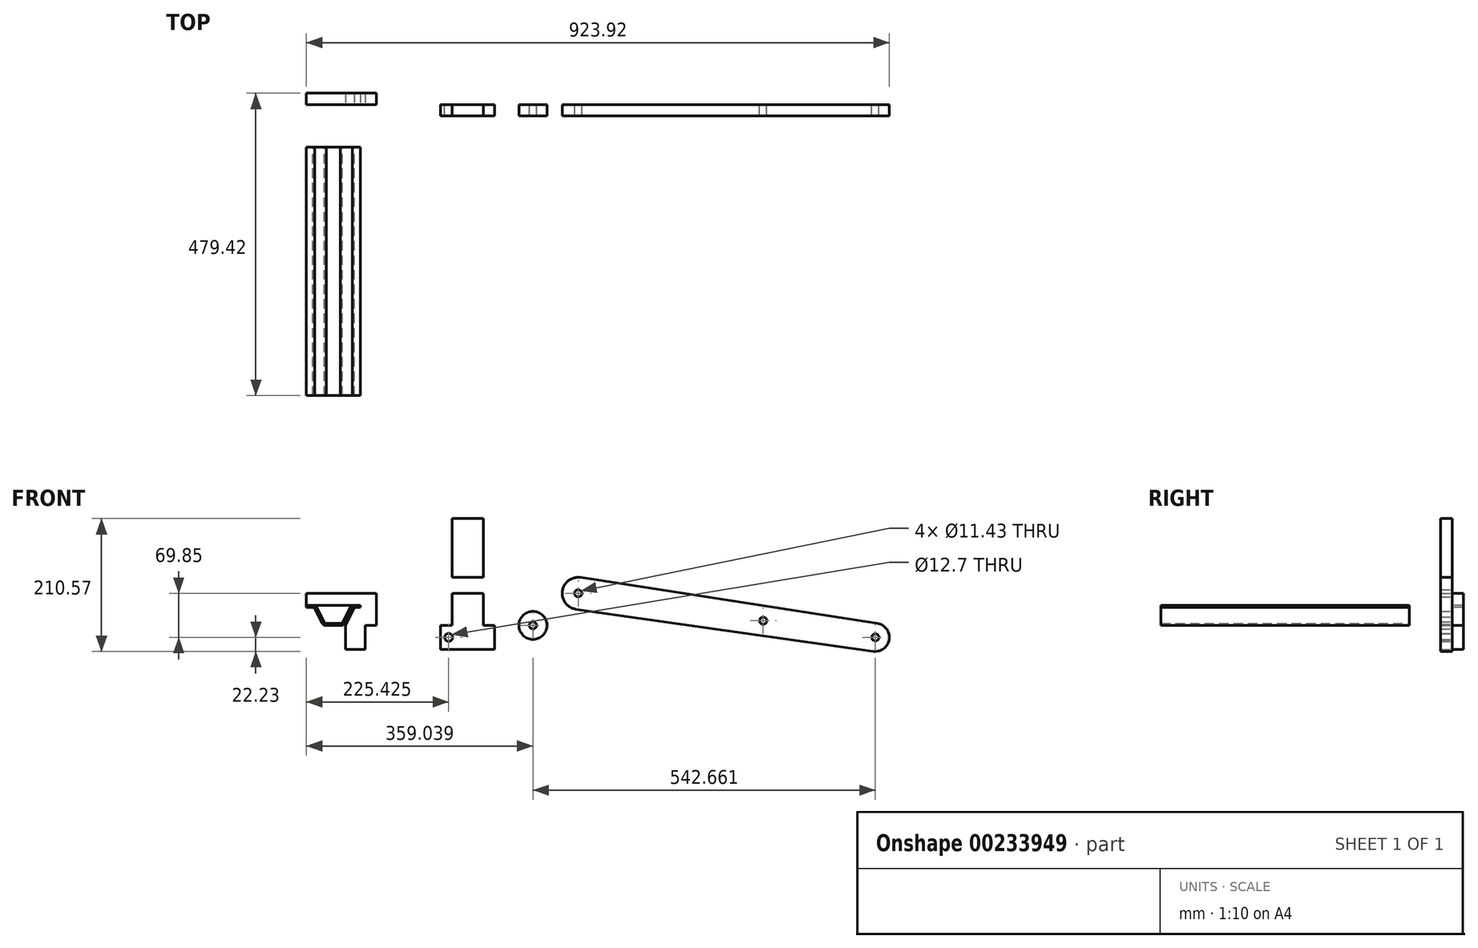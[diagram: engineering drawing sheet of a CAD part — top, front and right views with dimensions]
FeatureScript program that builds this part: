
annotation { "Feature Type Name" : "Feature", "Feature Type Description" : "" }
export const myFeature = defineFeature(function(context is Context, id is Id, definition is map)
    precondition{}
    {
        {
            var Q0;
            Q0=qCreatedBy(makeId("Top.planeOp"),FACE);
            var sketch = newSketch(context, id + "F0", { "sketchPlane" : qUnion([Q0])});
            skLineSegment(sketch, "E0.bottom", {"start": v(-241.3, 85.73) * mm, "end": v(-155.58, 85.73) * mm});
            skLineSegment(sketch, "E0.top", {"start": v(-241.3, 0) * mm, "end": v(-155.58, 0) * mm});
            skLineSegment(sketch, "E0.left", {"start": v(-241.3, 85.73) * mm, "end": v(-241.3, 0) * mm});
            skLineSegment(sketch, "E0.right", {"start": v(-155.58, 85.72) * mm, "end": v(-155.58, 0) * mm});
            skLineSegment(sketch, "E1", {"start": v(-212.73, 85.72) * mm, "end": v(-212.73, 0) * mm});
            skLineSegment(sketch, "E2", {"start": v(-184.15, 85.72) * mm, "end": v(-184.15, 0) * mm});
            skPoint(sketch, "E3", {"position": v(-198.44, 42.86) * mm});
            skPoint(sketch, "E3.positionSnap0", {"position": v(-198.44, 85.73) * mm});
            skPoint(sketch, "E3.positionSnap1", {"position": v(-241.3, 42.86) * mm});
            skLineSegment(sketch, "E4.bottom", {"start": v(-236.54, 52.39) * mm, "end": v(-231.2, 52.39) * mm});
            skLineSegment(sketch, "E4.top", {"start": v(-236.54, 42.86) * mm, "end": v(-231.2, 42.86) * mm});
            skLineSegment(sketch, "E4.left", {"start": v(-236.54, 52.39) * mm, "end": v(-236.54, 42.86) * mm});
            skLineSegment(sketch, "E4.right", {"start": v(-231.2, 52.39) * mm, "end": v(-231.2, 42.86) * mm});
            skLineSegment(sketch, "E5", {"start": v(-228.35, 85.73) * mm, "end": v(-228.35, 0) * mm});
            skLineSegment(sketch, "E6", {"start": v(-198.44, 85.73) * mm, "end": v(-198.44, 0) * mm, "construction": true});
            skLineSegment(sketch, "E7.MirrorCS", {"start": v(-165.67, 52.39) * mm, "end": v(-165.67, 42.86) * mm});
            skLineSegment(sketch, "E8.MirrorCS", {"start": v(-160.34, 52.39) * mm, "end": v(-160.34, 42.86) * mm});
            skPoint(sketch, "E9.MirrorP", {"position": v(-155.58, 42.86) * mm});
            skLineSegment(sketch, "E10.MirrorCS", {"start": v(-160.34, 52.39) * mm, "end": v(-165.67, 52.39) * mm});
            skLineSegment(sketch, "E11.MirrorCS", {"start": v(-160.34, 42.86) * mm, "end": v(-165.67, 42.86) * mm});
            skSolve(sketch);
        }
        {
            var Q0;
            {var subQ1=sQuery(id+"F0.wireOp",EDGE,"E0.left");Q0=makeQuery(id+"F0.imprint","IMPRINT",FACE,{"disambiguationData":[TD([[makeQuery(id+"F0.imprint","IMPRINT",EDGE,{"derivedFrom":subQ1}),1.0]])]});}
            var Q1;
            {var subQ0=sQuery(id+"F0.wireOp",EDGE,"E1");Q1=makeQuery(id+"F0.imprint","IMPRINT",FACE,{"disambiguationData":[TD([[makeQuery(id+"F0.imprint","IMPRINT",EDGE,{"derivedFrom":subQ0}),-1.0]])]});}
            var Q2;
            {var subQ0=sQuery(id+"F0.wireOp",EDGE,"E1");Q2=makeQuery(id+"F0.imprint","IMPRINT",FACE,{"disambiguationData":[TD([[makeQuery(id+"F0.imprint","IMPRINT",EDGE,{"derivedFrom":subQ0}),1.0]])]});}
            var Q3;
            {var subQ0=sQuery(id+"F0.wireOp",EDGE,"E0.right");Q3=makeQuery(id+"F0.imprint","IMPRINT",FACE,{"disambiguationData":[TD([[makeQuery(id+"F0.imprint","IMPRINT",EDGE,{"derivedFrom":subQ0}),-1.0]])]});}
            extrude(context, id + "F1", {"entities" : qUnion([Q0, Q1, Q2, Q3]), "depth" : 31.75 * mm});
        }
        {
            var Q0;
            Q0=makeQuery(id+"F1.opExtrude","SWEPT_FACE",FACE,{"disambiguationData":[OSD([sQuery(id+"F0.wireOp",EDGE,"E0.top")])]});
            var sketch = newSketch(context, id + "F2", { "sketchPlane" : qUnion([Q0])});
            skLineSegment(sketch, "E12", {"start": v(-241.3, 3.17) * mm, "end": v(-155.58, 3.18) * mm});
            skLineSegment(sketch, "E13", {"start": v(-241.3, 28.57) * mm, "end": v(-155.58, 28.57) * mm});
            skLineSegment(sketch, "E14", {"start": v(-228.35, 31.75) * mm, "end": v(-228.35, 28.57) * mm});
            skLineSegment(sketch, "E15", {"start": v(-212.73, 0) * mm, "end": v(-212.73, 3.17) * mm});
            skLineSegment(sketch, "E16", {"start": v(-198.44, 31.75) * mm, "end": v(-198.44, 0) * mm, "construction": true});
            skLineSegment(sketch, "E17.MirrorCS", {"start": v(-184.15, 0) * mm, "end": v(-184.15, 3.17) * mm});
            skLineSegment(sketch, "E18.MirrorCS", {"start": v(-168.53, 31.75) * mm, "end": v(-168.53, 28.57) * mm});
            skCircle(sketch, "E19", {"center": v(-228.35, 28.57) * mm, "radius": 3.18 * mm, "construction": true});
            skPoint(sketch, "E20", {"position": v(-231.52, 28.57) * mm});
            skCircle(sketch, "E21", {"center": v(-212.73, 3.17) * mm, "radius": 3.17 * mm, "construction": true});
            skPoint(sketch, "E22", {"position": v(-209.55, 3.17) * mm});
            skLineSegment(sketch, "E23", {"start": v(-227.23, 25.6) * mm, "end": v(-215.9, 3.17) * mm});
            skLineSegment(sketch, "E24", {"start": v(-225.17, 28.57) * mm, "end": v(-213.84, 6.15) * mm});
            skArc(sketch, "E25", {"start": v(-225.17, 28.57) * mm, "mid": v(-226.5, 30.42) * mm, "end": v(-228.35, 31.75) * mm});
            skArc(sketch, "E26", {"start": v(-215.9, 3.17) * mm, "mid": v(-214.57, 1.33) * mm, "end": v(-212.73, 0) * mm});
            skArc(sketch, "E27", {"start": v(-213.84, 6.15) * mm, "mid": v(-212.07, 4.12) * mm, "end": v(-209.55, 3.18) * mm});
            skArc(sketch, "E28", {"start": v(-227.23, 25.6) * mm, "mid": v(-229, 27.63) * mm, "end": v(-231.52, 28.57) * mm});
            skLineSegment(sketch, "E29.MirrorCS", {"start": v(-171.7, 28.57) * mm, "end": v(-183.03, 6.15) * mm});
            skArc(sketch, "E30.MirrorCS", {"start": v(-169.65, 25.6) * mm, "mid": v(-167.88, 27.63) * mm, "end": v(-165.35, 28.57) * mm});
            skArc(sketch, "E31.MirrorCS", {"start": v(-171.7, 28.57) * mm, "mid": v(-170.37, 30.42) * mm, "end": v(-168.53, 31.75) * mm});
            skArc(sketch, "E32.MirrorCS", {"start": v(-183.03, 6.15) * mm, "mid": v(-184.8, 4.12) * mm, "end": v(-187.33, 3.18) * mm});
            skArc(sketch, "E33.MirrorCS", {"start": v(-180.98, 3.17) * mm, "mid": v(-182.3, 1.33) * mm, "end": v(-184.15, 0) * mm});
            skLineSegment(sketch, "E34.MirrorCS", {"start": v(-169.65, 25.6) * mm, "end": v(-180.98, 3.17) * mm});
            skSolve(sketch);
        }
        {
            var Q0;
            {var subQ0=sQuery(id+"F2.wireOp",EDGE,"E14");Q0=makeQuery(id+"F2.imprint","IMPRINT",FACE,{"disambiguationData":[TD([[makeQuery(id+"F2.imprint","IMPRINT",EDGE,{"derivedFrom":subQ0}),-1.0]])]});}
            var Q1;
            {var subQ0=sQuery(id+"F2.wireOp",EDGE,"E14");Q1=makeQuery(id+"F2.imprint","IMPRINT",FACE,{"disambiguationData":[TD([[makeQuery(id+"F2.imprint","IMPRINT",EDGE,{"derivedFrom":subQ0}),1.0]])]});}
            var Q2;
            {var subQ7=sQuery(id+"F2.wireOp",EDGE,"E23");Q2=makeQuery(id+"F2.imprint","IMPRINT",FACE,{"disambiguationData":[TD([[makeQuery(id+"F2.imprint","IMPRINT",EDGE,{"derivedFrom":subQ7}),1.0]])]});}
            var Q3;
            {var subQ0=sQuery(id+"F2.wireOp",EDGE,"E15");Q3=makeQuery(id+"F2.imprint","IMPRINT",FACE,{"disambiguationData":[TD([[makeQuery(id+"F2.imprint","IMPRINT",EDGE,{"derivedFrom":subQ0}),-1.0]])]});}
            var Q4;
            {var subQ0=sQuery(id+"F2.wireOp",EDGE,"E15");Q4=makeQuery(id+"F2.imprint","IMPRINT",FACE,{"disambiguationData":[TD([[makeQuery(id+"F2.imprint","IMPRINT",EDGE,{"derivedFrom":subQ0}),1.0]])]});}
            var Q5;
            {var subQ0=sQuery(id+"F2.wireOp",EDGE,"E17.MirrorCS");Q5=makeQuery(id+"F2.imprint","IMPRINT",FACE,{"disambiguationData":[TD([[makeQuery(id+"F2.imprint","IMPRINT",EDGE,{"derivedFrom":subQ0}),-1.0]])]});}
            var Q6;
            {var subQ2=sQuery(id+"F2.wireOp",EDGE,"E29.MirrorCS");Q6=makeQuery(id+"F2.imprint","IMPRINT",FACE,{"disambiguationData":[TD([[makeQuery(id+"F2.imprint","IMPRINT",EDGE,{"derivedFrom":subQ2}),1.0]])]});}
            var Q7;
            {var subQ0=sQuery(id+"F2.wireOp",EDGE,"E18.MirrorCS");Q7=makeQuery(id+"F2.imprint","IMPRINT",FACE,{"disambiguationData":[TD([[makeQuery(id+"F2.imprint","IMPRINT",EDGE,{"derivedFrom":subQ0}),-1.0]])]});}
            var Q8;
            {var subQ7=sQuery(id+"F2.wireOp",EDGE,"E18.MirrorCS");Q8=makeQuery(id+"F2.imprint","IMPRINT",FACE,{"disambiguationData":[TD([[makeQuery(id+"F2.imprint","IMPRINT",EDGE,{"derivedFrom":subQ7}),1.0]])]});}
            extrude(context, id + "F3", {"entities" : qUnion([Q0, Q1, Q2, Q3, Q4, Q5, Q6, Q7, Q8]), "operationType" : NewBodyOperationType.INTERSECT, "endBound" : BoundingType.THROUGH_ALL, "oppositeDirection" : true, "depth" : 25.4 * mm});
        }
        {
            var Q0;
            Q0=qCreatedBy(makeId("Top.planeOp"),FACE);
            var sketch = newSketch(context, id + "F4", { "sketchPlane" : qUnion([Q0])});
            skLineSegment(sketch, "E35.bottom", {"start": v(-241.3, 85.72) * mm, "end": v(-130.17, 85.72) * mm});
            skLineSegment(sketch, "E35.top", {"start": v(-241.3, 67.7) * mm, "end": v(-130.17, 67.7) * mm});
            skLineSegment(sketch, "E35.left", {"start": v(-241.3, 85.72) * mm, "end": v(-241.3, 67.7) * mm});
            skLineSegment(sketch, "E35.right", {"start": v(-130.17, 85.72) * mm, "end": v(-130.17, 67.7) * mm});
            skSolve(sketch);
        }
        {
            var Q0;
            Q0=makeQuery(id+"F4.imprint","IMPRINT",FACE,{"disambiguationData":[TD([[makeQuery(id+"F4.imprint","IMPRINT",EDGE,{"derivedFrom":sQuery(id+"F4.wireOp",EDGE,"E35.bottom")}),-1.0]])]});
            extrude(context, id + "F5", {"entities" : qUnion([Q0]), "depth" : 50.8 * mm, "hasSecondDirection" : true, "secondDirectionOppositeDirection" : true, "secondDirectionDepth" : 38.1 * mm});
        }
        {
            var Q0;
            Q0=makeQuery(id+"F5.opExtrude","SWEPT_FACE",FACE,{"disambiguationData":[OSD([sQuery(id+"F4.wireOp",EDGE,"E35.top")])]});
            var sketch = newSketch(context, id + "F6", { "sketchPlane" : qUnion([Q0])});
            skLineSegment(sketch, "E36", {"start": v(-241.3, 31.75) * mm, "end": v(-155.58, 31.75) * mm});
            skLineSegment(sketch, "E37", {"start": v(-155.58, 31.75) * mm, "end": v(-155.58, 28.45) * mm});
            skLineSegment(sketch, "E38", {"start": v(-155.58, 28.45) * mm, "end": v(-165.1, 28.45) * mm});
            skLineSegment(sketch, "E39", {"start": v(-165.1, 28.45) * mm, "end": v(-179.47, 0) * mm});
            skLineSegment(sketch, "E40", {"start": v(-179.47, 0) * mm, "end": v(-179.47, -38.1) * mm});
            skLineSegment(sketch, "E41", {"start": v(-148.2, -38.1) * mm, "end": v(-148.2, 0) * mm});
            skLineSegment(sketch, "E42", {"start": v(-148.2, 0) * mm, "end": v(-130.17, 0) * mm});
            skLineSegment(sketch, "E43.bottom", {"start": v(-28.57, 50.8) * mm, "end": v(57.15, 50.8) * mm});
            skLineSegment(sketch, "E43.top", {"start": v(-28.57, -38.1) * mm, "end": v(57.15, -38.1) * mm});
            skLineSegment(sketch, "E43.left", {"start": v(-28.57, 50.8) * mm, "end": v(-28.57, -38.1) * mm});
            skLineSegment(sketch, "E43.right", {"start": v(57.15, 50.8) * mm, "end": v(57.15, -38.1) * mm});
            skLineSegment(sketch, "E44", {"start": v(-28.57, 0) * mm, "end": v(-10.54, 0) * mm});
            skLineSegment(sketch, "E45", {"start": v(-10.54, 0) * mm, "end": v(-10.54, 50.8) * mm});
            skLineSegment(sketch, "E46", {"start": v(57.15, 0) * mm, "end": v(39.12, 0) * mm});
            skLineSegment(sketch, "E47", {"start": v(39.12, 0) * mm, "end": v(39.12, 50.8) * mm});
            skCircle(sketch, "E48", {"center": v(-15.87, -19.05) * mm, "radius": 6.35 * mm});
            skPoint(sketch, "E48.centerSnap0", {"position": v(-148.2, -19.05) * mm});
            skPoint(sketch, "E48.centerSnap1", {"position": v(14.29, -38.1) * mm});
            skLineSegment(sketch, "E49.bottom", {"start": v(39.12, 76.2) * mm, "end": v(-10.54, 76.2) * mm});
            skLineSegment(sketch, "E49.top", {"start": v(39.12, 169.3) * mm, "end": v(-10.54, 169.3) * mm});
            skLineSegment(sketch, "E49.left", {"start": v(39.12, 76.2) * mm, "end": v(39.12, 169.3) * mm});
            skLineSegment(sketch, "E49.right", {"start": v(-10.54, 76.2) * mm, "end": v(-10.54, 169.3) * mm});
            skLineSegment(sketch, "E50", {"start": v(304.8, 0) * mm, "end": v(304.8, -19.05) * mm, "construction": true});
            skLineSegment(sketch, "E51", {"start": v(304.8, -19.05) * mm, "end": v(660.4, -19.05) * mm, "construction": true});
            skLineSegment(sketch, "E52", {"start": v(660.4, -19.05) * mm, "end": v(189.52, 50.8) * mm, "construction": true});
            skLineSegment(sketch, "E53", {"start": v(304.8, -19.05) * mm, "end": v(775.68, 50.8) * mm, "construction": true});
            skLineSegment(sketch, "E54", {"start": v(304.8, 0) * mm, "end": v(660.4, 0) * mm, "construction": true});
            skLineSegment(sketch, "E55", {"start": v(660.4, 0) * mm, "end": v(660.4, -50.8) * mm, "construction": true});
            skLineSegment(sketch, "E56", {"start": v(189.52, 50.8) * mm, "end": v(775.68, 50.8) * mm, "construction": true});
            skLineSegment(sketch, "E57", {"start": v(304.8, 50.8) * mm, "end": v(660.4, 50.8) * mm, "construction": true});
            skLineSegment(sketch, "E58", {"start": v(511.18, 0) * mm, "end": v(511.18, -50.8) * mm, "construction": true});
            skLineSegment(sketch, "E59", {"start": v(-28.57, -38.1) * mm, "end": v(-60.32, -38.1) * mm});
            skPoint(sketch, "E60", {"position": v(482.6, 7.32) * mm});
            skCircle(sketch, "E61", {"center": v(660.4, -19.05) * mm, "radius": 22.23 * mm});
            skCircle(sketch, "E62", {"center": v(189.52, 50.8) * mm, "radius": 25.4 * mm});
            skLineSegment(sketch, "E63", {"start": v(663.8, 2.91) * mm, "end": v(193.41, 75.9) * mm});
            skLineSegment(sketch, "E64", {"start": v(185.96, 25.65) * mm, "end": v(657.29, -41.06) * mm});
            skCircle(sketch, "E65", {"center": v(189.52, 50.8) * mm, "radius": 5.72 * mm});
            skCircle(sketch, "E66", {"center": v(660.4, -19.05) * mm, "radius": 5.72 * mm});
            skCircle(sketch, "E67", {"center": v(482.6, 7.32) * mm, "radius": 5.72 * mm});
            skCircle(sketch, "E68", {"center": v(117.74, 0) * mm, "radius": 22.23 * mm});
            skPoint(sketch, "E68.centerSnap0", {"position": v(48.13, 0) * mm});
            skCircle(sketch, "E69", {"center": v(117.74, 0) * mm, "radius": 5.72 * mm});
            skSolve(sketch);
        }
        {
            var Q0;
            {var subQ3=sQuery(id+"F6.wireOp",EDGE,"E36");Q0=makeQuery(id+"F6.imprint","IMPRINT",FACE,{"disambiguationData":[TD([[makeQuery(id+"F6.imprint","IMPRINT",EDGE,{"derivedFrom":subQ3}),1.0]])]});}
            extrude(context, id + "F7", {"entities" : qUnion([Q0]), "operationType" : NewBodyOperationType.INTERSECT, "oppositeDirection" : true, "depth" : 18.03 * mm});
        }
        {
            var Q0;
            {var subQ1=sQuery(id+"F6.wireOp",EDGE,"E43.top");Q0=makeQuery(id+"F6.imprint","IMPRINT",FACE,{"disambiguationData":[TD([[makeQuery(id+"F6.imprint","IMPRINT",EDGE,{"derivedFrom":subQ1}),1.0]])]});}
            var Q1;
            Q1=makeQuery(id+"F6.imprint","IMPRINT",FACE,{"disambiguationData":[TD([[makeQuery(id+"F6.imprint","IMPRINT",EDGE,{"derivedFrom":sQuery(id+"F6.wireOp",EDGE,"E49.bottom")}),-1.0]])]});
            var Q2;
            Q2=makeQuery(id+"F6.imprint","IMPRINT",FACE,{"disambiguationData":[TD([[makeQuery(id+"F6.imprint","IMPRINT",EDGE,{"derivedFrom":sQuery(id+"F6.wireOp",EDGE,"E65")}),-1.0]])]});
            var Q3;
            {var subQ0=sQuery(id+"F6.wireOp",EDGE,"E63");Q3=makeQuery(id+"F6.imprint","IMPRINT",FACE,{"disambiguationData":[TD([[makeQuery(id+"F6.imprint","IMPRINT",EDGE,{"derivedFrom":subQ0}),1.0]])]});}
            var Q4;
            Q4=makeQuery(id+"F6.imprint","IMPRINT",FACE,{"disambiguationData":[TD([[makeQuery(id+"F6.imprint","IMPRINT",EDGE,{"derivedFrom":sQuery(id+"F6.wireOp",EDGE,"E66")}),-1.0]])]});
            var Q5;
            Q5=makeQuery(id+"F6.imprint","IMPRINT",FACE,{"disambiguationData":[TD([[makeQuery(id+"F6.imprint","IMPRINT",EDGE,{"derivedFrom":sQuery(id+"F6.wireOp",EDGE,"E68")}),1.0]])]});
            extrude(context, id + "F8", {"entities" : qUnion([Q0, Q1, Q2, Q3, Q4, Q5]), "depth" : 18.03 * mm});
        }
        {
            var Q0;
            {var subQ7=sQuery(id+"F2.wireOp",EDGE,"E18.MirrorCS");Q0=makeQuery(id+"F2.imprint","IMPRINT",FACE,{"disambiguationData":[TD([[makeQuery(id+"F2.imprint","IMPRINT",EDGE,{"derivedFrom":subQ7}),1.0]])]});}
            var Q1;
            {var subQ0=sQuery(id+"F2.wireOp",EDGE,"E18.MirrorCS");Q1=makeQuery(id+"F2.imprint","IMPRINT",FACE,{"disambiguationData":[TD([[makeQuery(id+"F2.imprint","IMPRINT",EDGE,{"derivedFrom":subQ0}),-1.0]])]});}
            var Q2;
            {var subQ2=sQuery(id+"F2.wireOp",EDGE,"E29.MirrorCS");Q2=makeQuery(id+"F2.imprint","IMPRINT",FACE,{"disambiguationData":[TD([[makeQuery(id+"F2.imprint","IMPRINT",EDGE,{"derivedFrom":subQ2}),1.0]])]});}
            var Q3;
            {var subQ0=sQuery(id+"F2.wireOp",EDGE,"E14");Q3=makeQuery(id+"F2.imprint","IMPRINT",FACE,{"disambiguationData":[TD([[makeQuery(id+"F2.imprint","IMPRINT",EDGE,{"derivedFrom":subQ0}),-1.0]])]});}
            var Q4;
            {var subQ0=sQuery(id+"F2.wireOp",EDGE,"E14");Q4=makeQuery(id+"F2.imprint","IMPRINT",FACE,{"disambiguationData":[TD([[makeQuery(id+"F2.imprint","IMPRINT",EDGE,{"derivedFrom":subQ0}),1.0]])]});}
            var Q5;
            {var subQ0=sQuery(id+"F2.wireOp",EDGE,"E15");Q5=makeQuery(id+"F2.imprint","IMPRINT",FACE,{"disambiguationData":[TD([[makeQuery(id+"F2.imprint","IMPRINT",EDGE,{"derivedFrom":subQ0}),-1.0]])]});}
            var Q6;
            {var subQ0=sQuery(id+"F2.wireOp",EDGE,"E17.MirrorCS");Q6=makeQuery(id+"F2.imprint","IMPRINT",FACE,{"disambiguationData":[TD([[makeQuery(id+"F2.imprint","IMPRINT",EDGE,{"derivedFrom":subQ0}),-1.0]])]});}
            var Q7;
            {var subQ0=sQuery(id+"F2.wireOp",EDGE,"E15");Q7=makeQuery(id+"F2.imprint","IMPRINT",FACE,{"disambiguationData":[TD([[makeQuery(id+"F2.imprint","IMPRINT",EDGE,{"derivedFrom":subQ0}),1.0]])]});}
            var Q8;
            {var subQ7=sQuery(id+"F2.wireOp",EDGE,"E23");Q8=makeQuery(id+"F2.imprint","IMPRINT",FACE,{"disambiguationData":[TD([[makeQuery(id+"F2.imprint","IMPRINT",EDGE,{"derivedFrom":subQ7}),1.0]])]});}
            extrude(context, id + "F9", {"entities" : qUnion([Q0, Q1, Q2, Q3, Q4, Q5, Q6, Q7, Q8]), "depth" : 393.7 * mm});
        }
    });
